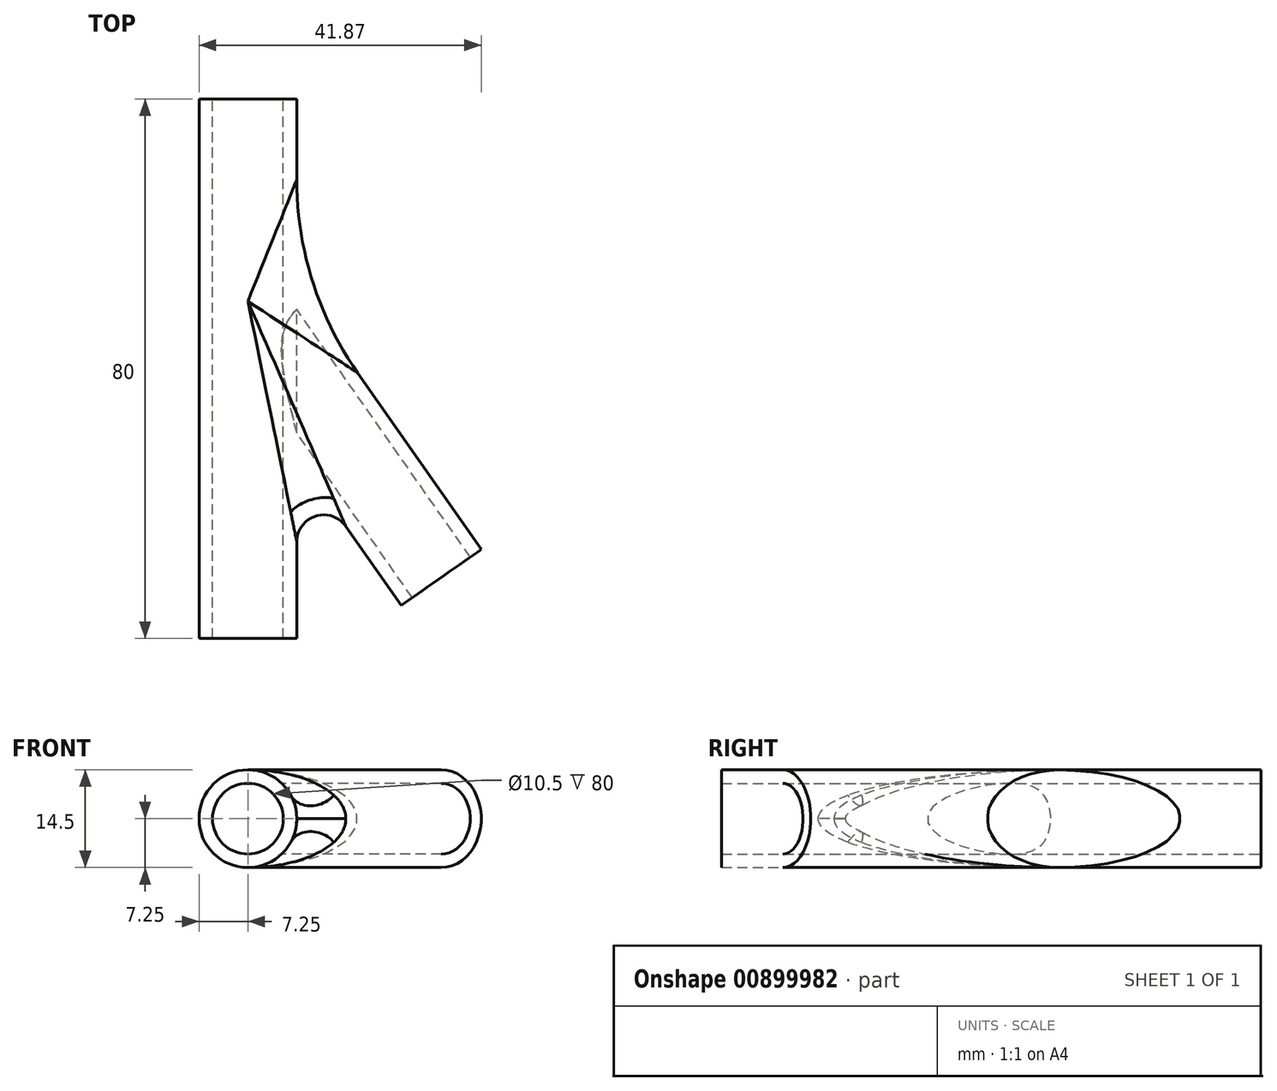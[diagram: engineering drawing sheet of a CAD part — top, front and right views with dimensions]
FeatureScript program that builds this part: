
annotation { "Feature Type Name" : "Feature", "Feature Type Description" : "" }
export const myFeature = defineFeature(function(context is Context, id is Id, definition is map)
    precondition{}
    {
        {
            assignVariable(context, id + "F0", {"name" : "angle", "anyValue" : 35});
        }
        {
            var Q0;
            Q0=qCreatedBy(makeId("Top.planeOp"),FACE);
            var sketch = newSketch(context, id + "F1", { "sketchPlane" : qUnion([Q0])});
            skCircle(sketch, "E0", {"center": v(0, 0) * mm, "radius": 77.94 * mm, "construction": true});
            skSolve(sketch);
        }
        {
            var Q0;
            Q0=qCreatedBy(makeId("Front.planeOp"),FACE);
            var sketch = newSketch(context, id + "F2", { "sketchPlane" : qUnion([Q0])});
            skCircle(sketch, "E1", {"center": v(0, 0) * mm, "radius": 7.25 * mm});
            skCircle(sketch, "E2", {"center": v(0, 0) * mm, "radius": 5.25 * mm});
            skSolve(sketch);
        }
        {
            var Q0;
            Q0=qSketchRegion(id+"F2",true);
            extrude(context, id + "F3", {"entities" : qUnion([Q0]), "depth" : 50 * mm, "offsetDistance" : 25 * mm});
        }
        {
            var Q0;
            Q0=makeQuery(id+"F3.opExtrude","SWEPT_BODY",BODY,{"disambiguationData":[OSD([sQuery(id+"F2.wireOp",EDGE,"E1"),sQuery(id+"F2.wireOp",EDGE,"E2")])]});
            var Q1;
            Q1=sQuery(id+"F1.wireOp",EDGE,"E0");
            circularPattern(context, id + "F4", {"operationType" : NewBodyOperationType.ADD, "entities" : qUnion([Q0]), "axis" : qUnion([Q1]), "angle" : (getVariable(context, 'angle')) * degree, "instanceCount" : 2, "equalSpace" : true});
        }
        {
            var Q0;
            Q0=qSketchRegion(id+"F2",true);
            extrude(context, id + "F5", {"entities" : qUnion([Q0]), "operationType" : NewBodyOperationType.ADD, "oppositeDirection" : true, "depth" : 30 * mm, "offsetDistance" : 25 * mm});
        }
        {
            var Q0;
            Q0=makeQuery(id+"F2.imprint","IMPRINT",FACE,{"disambiguationData":[TD([[makeQuery(id+"F2.imprint","IMPRINT",EDGE,{"derivedFrom":sQuery(id+"F2.wireOp",EDGE,"E2")}),1.0]])]});
            extrude(context, id + "F6", {"entities" : qUnion([Q0]), "operationType" : NewBodyOperationType.REMOVE, "endBound" : BoundingType.THROUGH_ALL, "depth" : 25 * mm, "offsetDistance" : 25 * mm});
        }
        {
            var Q0;
            Q0=makeQuery(id+"F2.imprint","IMPRINT",FACE,{"disambiguationData":[TD([[makeQuery(id+"F2.imprint","IMPRINT",EDGE,{"derivedFrom":sQuery(id+"F2.wireOp",EDGE,"E2")}),1.0]])]});
            extrude(context, id + "F7", {"entities" : qUnion([Q0]), "operationType" : NewBodyOperationType.REMOVE, "endBound" : BoundingType.THROUGH_ALL, "oppositeDirection" : true, "depth" : 25 * mm, "offsetDistance" : 25 * mm});
        }
        {
            var Q0;
            {var subQ0=makeQuery(id+"F3.opExtrude","SWEPT_FACE",FACE,{"disambiguationData":[OSD([sQuery(id+"F2.wireOp",EDGE,"E1")])]});Q0=makeQuery(id+"F4.boolean.opBoolean","INTERSECT",EDGE,{"derivedFrom":[subQ0,makeQuery(id+"F4.opPattern","COPY",FACE,{"derivedFrom":subQ0,"instanceName":"1"})]});}
            fillet(context, id + "F8", {"entities" : qUnion([Q0]), "radius" : 4 * mm, "tangentPropagation" : true, "allowEdgeOverflow" : false});
        }
        {
            var Q0;
            {var subQ0=sQuery(id+"F2.wireOp",EDGE,"E1");var subQ1=makeQuery(id+"F3.opExtrude","SWEPT_FACE",FACE,{"disambiguationData":[OSD([subQ0])]});Q0=makeQuery(id+"F5.boolean.opBoolean","INTERSECT",EDGE,{"derivedFrom":[makeQuery(id+"F4.boolean.opBoolean","SPLIT",FACE,{"disambiguationData":[TD([subQ1])],"derivedFrom":makeQuery(id+"F4.opPattern","COPY",FACE,{"derivedFrom":subQ1,"instanceName":"1"})}),makeQuery(id+"F5.opExtrude","SWEPT_FACE",FACE,{"disambiguationData":[OSD([subQ0])]})]});}
            fillet(context, id + "F9", {"entities" : qUnion([Q0]), "radius" : 50 * mm, "tangentPropagation" : true, "allowEdgeOverflow" : false});
        }
    });
